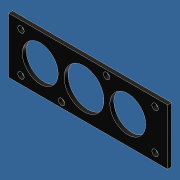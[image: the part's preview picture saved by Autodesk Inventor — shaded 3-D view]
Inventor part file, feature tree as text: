
AUTODESK INVENTOR PART (.ipt)
format: ipt  version: unknown  size: 218,112 bytes
history: native  units: in
note: dims shown in document units (in); Inventor stores cm internally (conversion verified against a paired STEP export)
features: sketch x5, extrude x3, hole x2, reference x2
ambient origin geometry x8: Origin, YZ Plane, XZ Plane, XY Plane, X Axis, Y Axis, Z Axis, Center Point
bodies: Solid1 (feature_tree)
feature tree (12):
  extrude  "Extrusion1"  Depth=1.75in
  extrude  "Extrusion2"  Depth=1.25in
  hole  "Hole1"  [1 undecoded]
  hole  "Hole2"  [1 undecoded]
  extrude  "Extrusion3"  Depth=0.25in
  sketch  "Sketch1"  dims[d0=5.0in d1=1.75in]
  sketch  "Sketch2"  dims[d2=0.125in d3=0.0in d4=1.25in]
  sketch  "Sketch3"  dims[d5=2.375in d6=0.875in]
  sketch  "Sketch4"  dims[d7=0.125in d8=0.0in d9=0.3937in]
  reference  "Reference1"
  reference  "Reference2"
  sketch  "Sketch5"  dims[d10=0.3937in d11=0.25in d12=0.25in d13=0.3937in d14=0.3937in d15=0.25in d16=0.25in d17=0.201in d18=0.75in d19=0.385in d20=0.25in d21=0.5635in d22=1.0in d23=0.8108in d24=0.201in d25=0.75in d26=0.385in d27=0.25in d28=0.5635in d29=1.0in d30=0.8108in d31=1.125in d32=0.875in d33=1.0in d34=1.125in d35=1.375in d36=0.875in d37=1.0in d38=0.0in]
note: 2 required parameter values undecoded (feature->parameter linkage not recoverable at this tier; creation-order binding heuristic only, values carry confidence <= 0.55)
